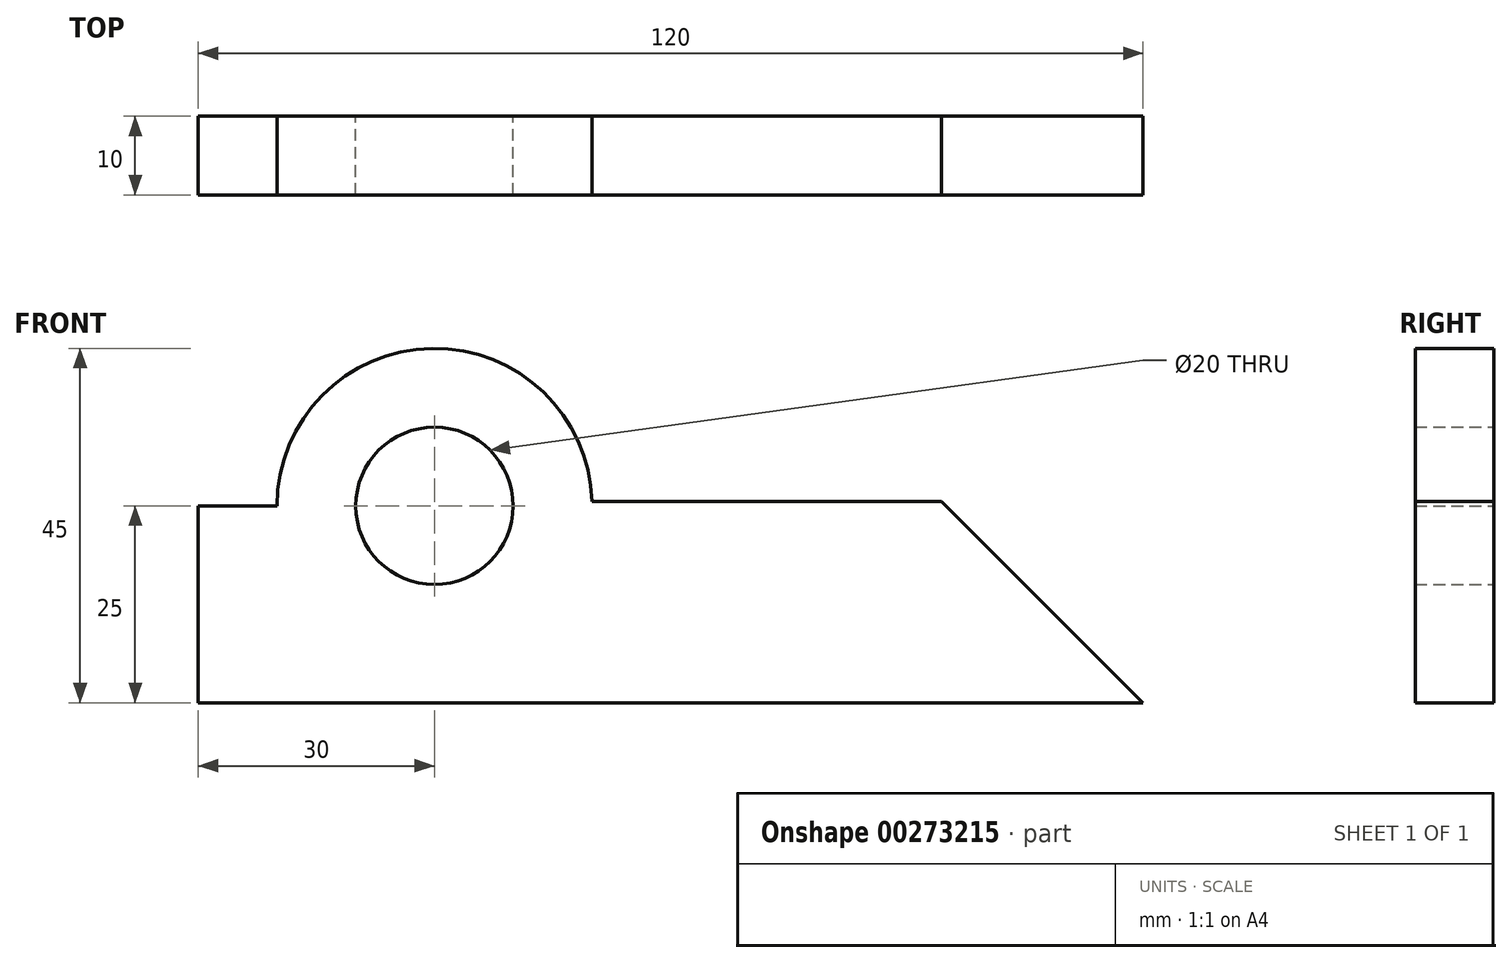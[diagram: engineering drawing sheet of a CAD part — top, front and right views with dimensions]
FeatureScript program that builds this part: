
annotation { "Feature Type Name" : "Feature", "Feature Type Description" : "" }
export const myFeature = defineFeature(function(context is Context, id is Id, definition is map)
    precondition{}
    {
        {
            var Q0;
            Q0=qCreatedBy(makeId("Front.planeOp"),FACE);
            var sketch = newSketch(context, id + "F0", { "sketchPlane" : qUnion([Q0])});
            skLineSegment(sketch, "E0", {"start": v(0, 0) * mm, "end": v(0, 25) * mm});
            skLineSegment(sketch, "E1", {"start": v(0, 25) * mm, "end": v(10, 25) * mm});
            skLineSegment(sketch, "E2", {"start": v(0, 0) * mm, "end": v(120, 0) * mm});
            skLineSegment(sketch, "E3", {"start": v(120, 0) * mm, "end": v(94.42, 25.58) * mm});
            skLineSegment(sketch, "E4", {"start": v(94.42, 25.58) * mm, "end": v(50, 25.58) * mm});
            skArc(sketch, "E5", {"start": v(50, 25.58) * mm, "mid": v(29.71, 45) * mm, "end": v(10, 25) * mm});
            skCircle(sketch, "E6", {"center": v(30, 25) * mm, "radius": 10 * mm});
            skSolve(sketch);
        }
        {
            var Q0;
            Q0 = qSketchRegion(id + "F0", true);
            extrude(context, id + "F1", {"entities" : qUnion([Q0]), "depth" : 10 * mm});
        }
    });
